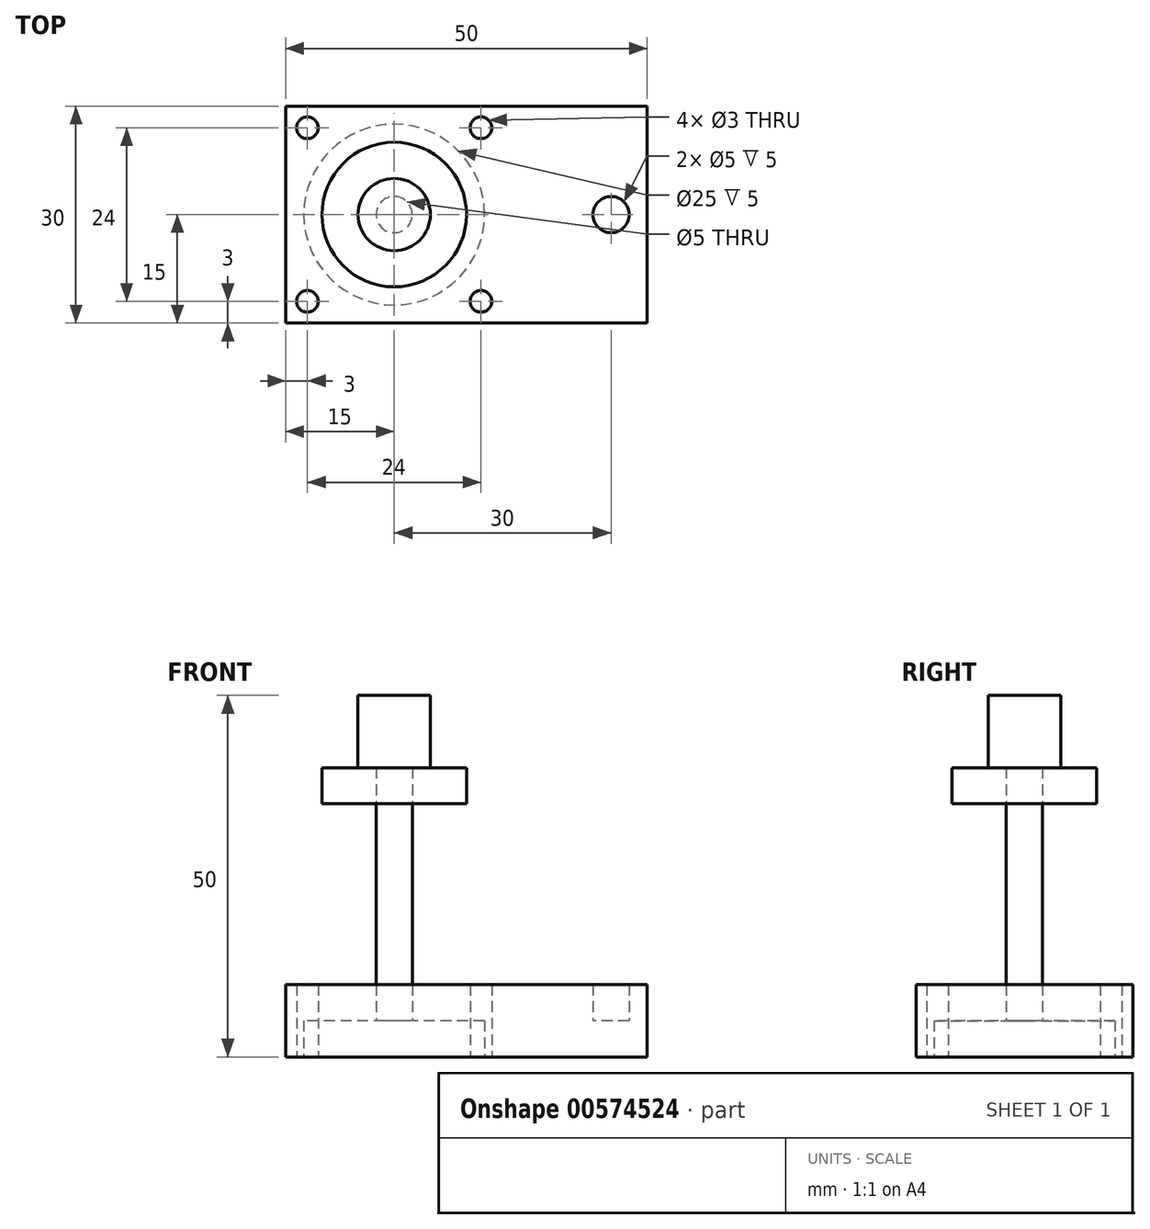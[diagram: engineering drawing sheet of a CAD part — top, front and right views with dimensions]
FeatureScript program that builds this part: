
annotation { "Feature Type Name" : "Feature", "Feature Type Description" : "" }
export const myFeature = defineFeature(function(context is Context, id is Id, definition is map)
    precondition{}
    {
        {
            var Q0;
            Q0=qCreatedBy(makeId("Top.planeOp"),FACE);
            var sketch = newSketch(context, id + "F0", { "sketchPlane" : qUnion([Q0])});
            skLineSegment(sketch, "E0.bottom", {"start": v(15, 15) * mm, "end": v(-15, 15) * mm});
            skLineSegment(sketch, "E0.top", {"start": v(15, -15) * mm, "end": v(-15, -15) * mm});
            skLineSegment(sketch, "E0.left", {"start": v(15, 15) * mm, "end": v(15, -15) * mm});
            skLineSegment(sketch, "E0.right", {"start": v(-15, 15) * mm, "end": v(-15, -15) * mm});
            skPoint(sketch, "E0.middle", {"position": v(0, 0) * mm});
            skLineSegment(sketch, "E1", {"start": v(-15, -12) * mm, "end": v(-12, -12) * mm});
            skLineSegment(sketch, "E2", {"start": v(15, -12) * mm, "end": v(12, -12) * mm});
            skLineSegment(sketch, "E3", {"start": v(15, 12) * mm, "end": v(12, 12) * mm});
            skLineSegment(sketch, "E4", {"start": v(-15, 12) * mm, "end": v(-12, 12) * mm});
            skCircle(sketch, "E5", {"center": v(-12, 12) * mm, "radius": 1.5 * mm});
            skCircle(sketch, "E6", {"center": v(12, 12) * mm, "radius": 1.5 * mm});
            skCircle(sketch, "E7", {"center": v(12, -12) * mm, "radius": 1.5 * mm});
            skCircle(sketch, "E8", {"center": v(-12, -12) * mm, "radius": 1.5 * mm});
            skCircle(sketch, "E9", {"center": v(0, 0) * mm, "radius": 12.5 * mm});
            skLineSegment(sketch, "E10", {"start": v(15, -15) * mm, "end": v(35, -15) * mm});
            skLineSegment(sketch, "E11", {"start": v(35, -15) * mm, "end": v(35, 15) * mm});
            skLineSegment(sketch, "E12", {"start": v(35, 15) * mm, "end": v(15, 15) * mm});
            skLineSegment(sketch, "E13", {"start": v(35, 0) * mm, "end": v(30, 0) * mm});
            skPoint(sketch, "E13.endSnap0", {"position": v(35, 0) * mm});
            skCircle(sketch, "E14", {"center": v(30, 0) * mm, "radius": 2.5 * mm});
            skSolve(sketch);
        }
        {
            var Q0;
            {var subQ4=sQuery(id+"F0.wireOp",EDGE,"E0.bottom");Q0=makeQuery(id+"F0.imprint","IMPRINT",FACE,{"disambiguationData":[TD([[makeQuery(id+"F0.imprint","IMPRINT",EDGE,{"derivedFrom":subQ4}),1.0]])]});}
            var Q1;
            {var subQ0=sQuery(id+"F0.wireOp",EDGE,"E10");Q1=makeQuery(id+"F0.imprint","IMPRINT",FACE,{"disambiguationData":[TD([[makeQuery(id+"F0.imprint","IMPRINT",EDGE,{"derivedFrom":subQ0}),1.0]])]});}
            var Q2;
            Q2=makeQuery(id+"F0.imprint","IMPRINT",FACE,{"disambiguationData":[TD([[makeQuery(id+"F0.imprint","IMPRINT",EDGE,{"derivedFrom":sQuery(id+"F0.wireOp",EDGE,"E14")}),1.0]])]});
            extrude(context, id + "F1", {"entities" : qUnion([Q0, Q1, Q2]), "depth" : 5 * mm, "offsetDistance" : 25 * mm});
        }
        {
            var Q0;
            Q0=makeQuery(id+"F1.opExtrude","CAP_FACE",FACE,{"disambiguationData":[OSD([sQuery(id+"F0.wireOp",EDGE,"E0.bottom"),sQuery(id+"F0.wireOp",EDGE,"E0.top"),sQuery(id+"F0.wireOp",EDGE,"E0.left"),sQuery(id+"F0.wireOp",EDGE,"E0.right"),sQuery(id+"F0.wireOp",EDGE,"E5"),sQuery(id+"F0.wireOp",EDGE,"E6"),sQuery(id+"F0.wireOp",EDGE,"E7"),sQuery(id+"F0.wireOp",EDGE,"E8"),sQuery(id+"F0.wireOp",EDGE,"E9")])],"isStart":false});
            var sketch = newSketch(context, id + "F2", { "sketchPlane" : qUnion([Q0])});
            skLineSegment(sketch, "E15.bottom", {"start": v(-15, 15) * mm, "end": v(15, 15) * mm});
            skLineSegment(sketch, "E15.top", {"start": v(-15, -15) * mm, "end": v(15, -15) * mm});
            skLineSegment(sketch, "E15.left", {"start": v(-15, 15) * mm, "end": v(-15, -15) * mm});
            skLineSegment(sketch, "E15.right", {"start": v(15, 15) * mm, "end": v(15, -15) * mm});
            skPoint(sketch, "E15.middle", {"position": v(0, 0) * mm});
            skCircle(sketch, "E16", {"center": v(0, 0) * mm, "radius": 2.5 * mm});
            skLineSegment(sketch, "E17", {"start": v(35, 0) * mm, "end": v(30, 0) * mm});
            skPoint(sketch, "E17.endSnap0", {"position": v(35, 0) * mm});
            skCircle(sketch, "E18", {"center": v(30, 0) * mm, "radius": 2.5 * mm});
            skSolve(sketch);
        }
        {
            var Q0;
            Q0=makeQuery(id+"F2.imprint","IMPRINT",FACE,{"disambiguationData":[TD([[makeQuery(id+"F2.imprint","IMPRINT",EDGE,{"derivedFrom":sQuery(id+"F2.wireOp",EDGE,"E15.bottom")}),1.0]])]});
            var Q1;
            Q1=makeQuery(id+"F2.imprint","IMPRINT",FACE,{"disambiguationData":[TD([[makeQuery(id+"F2.imprint","IMPRINT",EDGE,{"derivedFrom":sQuery(id+"F2.wireOp",EDGE,"E16")}),-1.0]])]});
            var Q2;
            {var subQ2=sQuery(id+"F2.wireOp",EDGE,"E15.right");Q2=makeQuery(id+"F2.imprint","IMPRINT",FACE,{"disambiguationData":[TD([[makeQuery(id+"F2.imprint","IMPRINT",EDGE,{"derivedFrom":subQ2}),1.0]])]});}
            extrude(context, id + "F3", {"entities" : qUnion([Q0, Q1, Q2]), "operationType" : NewBodyOperationType.ADD, "depth" : 5 * mm, "offsetDistance" : 25 * mm});
        }
        {
            var Q0;
            Q0=makeQuery(id+"F3.opExtrude","CAP_FACE",FACE,{"disambiguationData":[OSD([sQuery(id+"F0.wireOp",EDGE,"E5"),sQuery(id+"F0.wireOp",EDGE,"E6"),sQuery(id+"F0.wireOp",EDGE,"E7"),sQuery(id+"F0.wireOp",EDGE,"E8"),sQuery(id+"F2.wireOp",EDGE,"E15.bottom"),sQuery(id+"F2.wireOp",EDGE,"E15.top"),sQuery(id+"F2.wireOp",EDGE,"E15.left"),sQuery(id+"F2.wireOp",EDGE,"E15.right"),sQuery(id+"F2.wireOp",EDGE,"E16")])],"isStart":false});
            var sketch = newSketch(context, id + "F4", { "sketchPlane" : qUnion([Q0])});
            skCircle(sketch, "E19", {"center": v(0, 0) * mm, "radius": 2.5 * mm});
            skSolve(sketch);
        }
        {
            var Q0;
            Q0=makeQuery(id+"F4.imprint","IMPRINT",FACE,{"disambiguationData":[TD([[makeQuery(id+"F4.imprint","IMPRINT",EDGE,{"derivedFrom":sQuery(id+"F4.wireOp",EDGE,"E19")}),1.0]])]});
            extrude(context, id + "F5", {"entities" : qUnion([Q0]), "depth" : 25 * mm, "offsetDistance" : 25 * mm});
        }
        {
            var Q0;
            Q0=makeQuery(id+"F5.opExtrude","CAP_FACE",FACE,{"disambiguationData":[OSD([sQuery(id+"F4.wireOp",EDGE,"E19")])],"isStart":false});
            var sketch = newSketch(context, id + "F6", { "sketchPlane" : qUnion([Q0])});
            skCircle(sketch, "E20", {"center": v(0, 0) * mm, "radius": 10 * mm});
            skSolve(sketch);
        }
        {
            var Q0;
            Q0=makeQuery(id+"F6.imprint","IMPRINT",FACE,{"disambiguationData":[TD([[makeQuery(id+"F6.imprint","IMPRINT",EDGE,{"derivedFrom":sQuery(id+"F6.wireOp",EDGE,"E20")}),1.0]])]});
            extrude(context, id + "F7", {"entities" : qUnion([Q0]), "depth" : 5 * mm, "offsetDistance" : 25 * mm});
        }
        {
            var Q0;
            Q0=makeQuery(id+"F7.opExtrude","CAP_FACE",FACE,{"disambiguationData":[OSD([sQuery(id+"F4.wireOp",EDGE,"E19"),sQuery(id+"F6.wireOp",EDGE,"E20")])],"isStart":false});
            var sketch = newSketch(context, id + "F8", { "sketchPlane" : qUnion([Q0])});
            skCircle(sketch, "E21", {"center": v(0, 0) * mm, "radius": 5 * mm});
            skSolve(sketch);
        }
        {
            var Q0;
            Q0=makeQuery(id+"F8.imprint","IMPRINT",FACE,{"disambiguationData":[TD([[makeQuery(id+"F8.imprint","IMPRINT",EDGE,{"derivedFrom":sQuery(id+"F8.wireOp",EDGE,"E21")}),1.0]])]});
            var Q1;
            Q1=makeQuery(id+"F8.imprint","IMPRINT",FACE,{"disambiguationData":[TD([[makeQuery(id+"F8.imprint","IMPRINT",EDGE,{"derivedFrom":makeQuery(id+"F7.opExtrude","CAP_EDGE",EDGE,{"disambiguationData":[OSD([sQuery(id+"F4.wireOp",EDGE,"E19")])],"isStart":false})}),1.0]])]});
            extrude(context, id + "F9", {"entities" : qUnion([Q0, Q1]), "operationType" : NewBodyOperationType.ADD, "depth" : 10 * mm, "offsetDistance" : 25 * mm});
        }
    });
